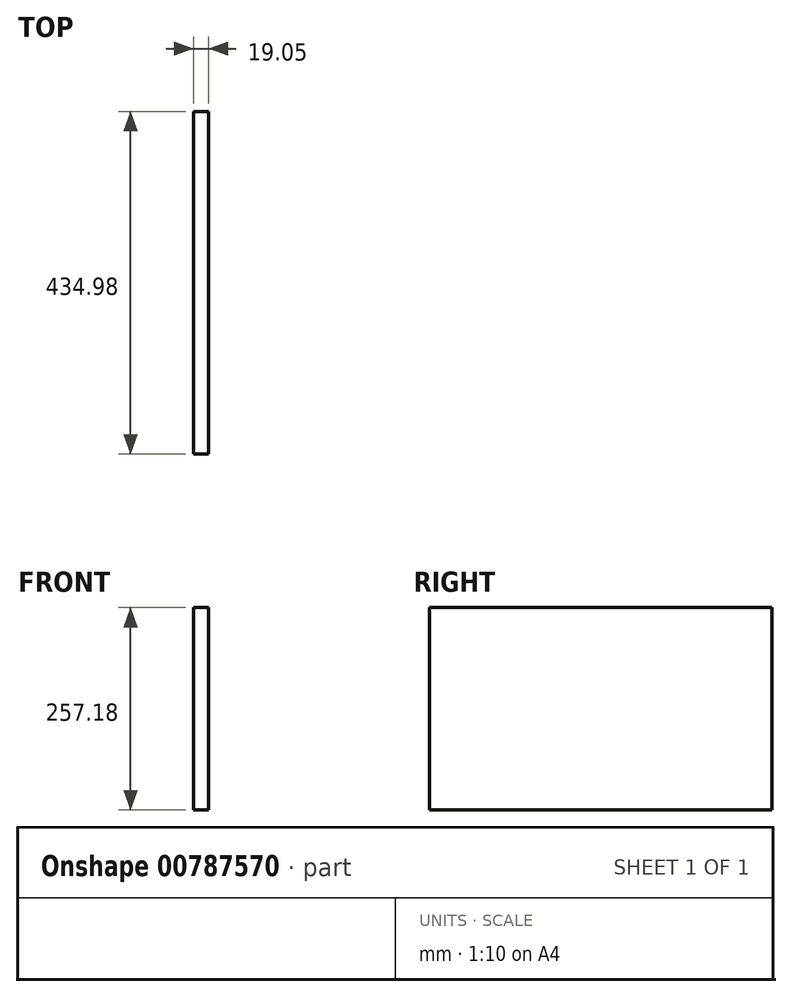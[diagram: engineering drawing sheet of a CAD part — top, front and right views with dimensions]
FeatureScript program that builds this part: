
annotation { "Feature Type Name" : "Feature", "Feature Type Description" : "" }
export const myFeature = defineFeature(function(context is Context, id is Id, definition is map)
    precondition{}
    {
        {
            var Q0;
            Q0=qCreatedBy(makeId("Right.planeOp"),FACE);
            var sketch = newSketch(context, id + "F0", { "sketchPlane" : qUnion([Q0])});
            skLineSegment(sketch, "E0.bottom", {"start": v(217.49, 128.59) * mm, "end": v(-217.49, 128.59) * mm});
            skLineSegment(sketch, "E0.top", {"start": v(217.49, -128.59) * mm, "end": v(-217.49, -128.59) * mm});
            skLineSegment(sketch, "E0.left", {"start": v(217.49, 128.59) * mm, "end": v(217.49, -128.59) * mm});
            skLineSegment(sketch, "E0.right", {"start": v(-217.49, 128.59) * mm, "end": v(-217.49, -128.59) * mm});
            skPoint(sketch, "E0.middle", {"position": v(0, 0) * mm});
            skSolve(sketch);
        }
        {
            var Q0;
            Q0=makeQuery(id+"F0.imprint","IMPRINT",FACE,{"disambiguationData":[TD([[makeQuery(id+"F0.imprint","IMPRINT",EDGE,{"derivedFrom":sQuery(id+"F0.wireOp",EDGE,"E0.bottom")}),1.0]])]});
            extrude(context, id + "F1", {"entities" : qUnion([Q0]), "depth" : 19.05 * mm, "offsetDistance" : 25.4 * mm});
        }
    });
